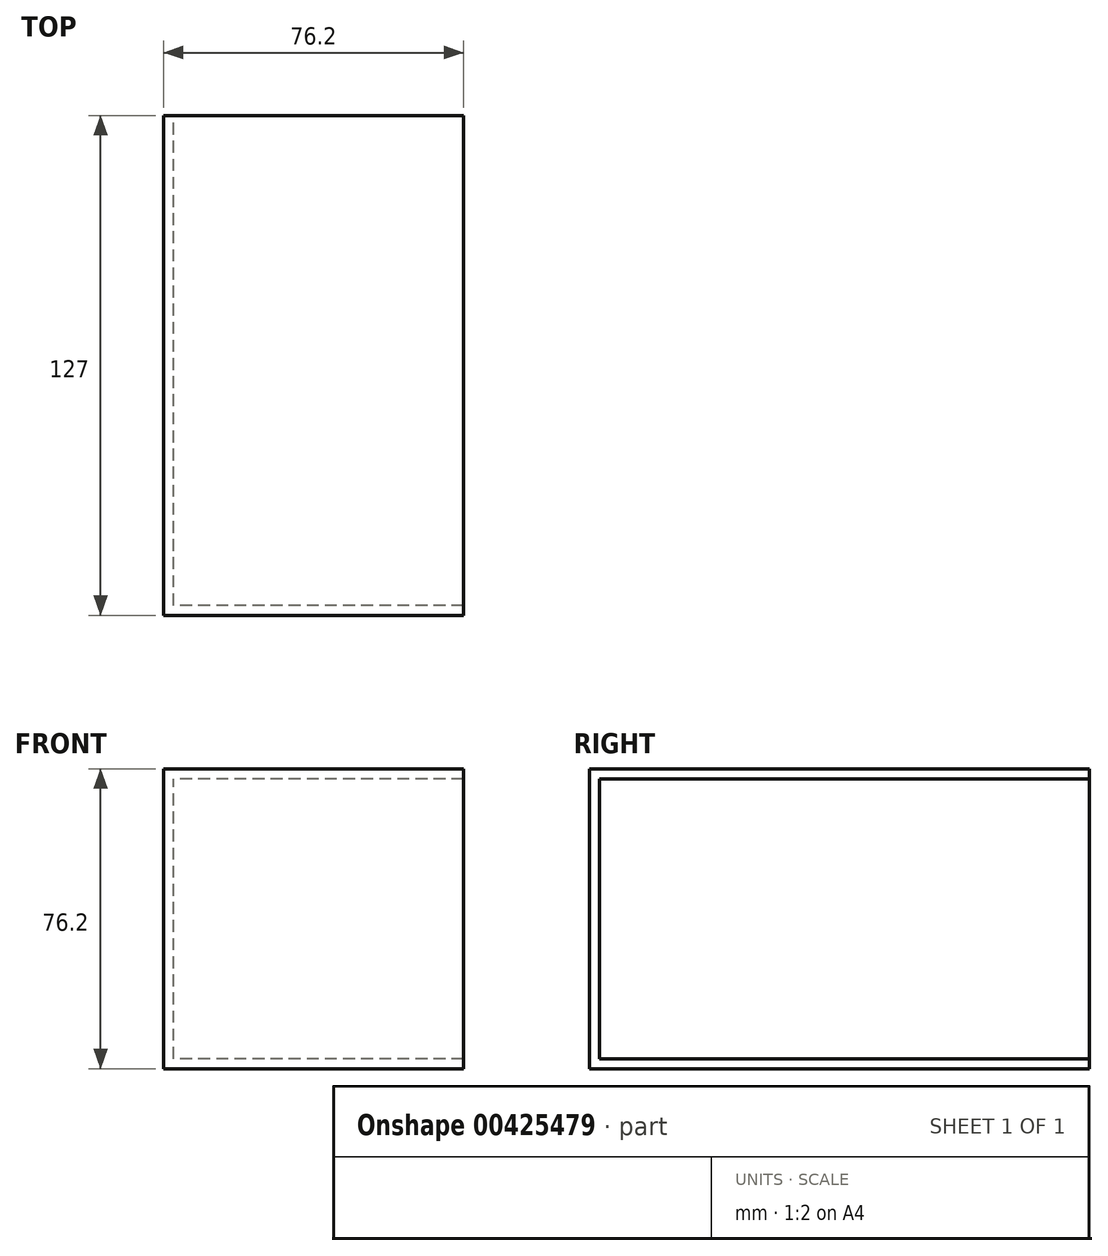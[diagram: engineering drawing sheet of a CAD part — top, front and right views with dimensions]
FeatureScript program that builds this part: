
annotation { "Feature Type Name" : "Feature", "Feature Type Description" : "" }
export const myFeature = defineFeature(function(context is Context, id is Id, definition is map)
    precondition{}
    {
        {
            var Q0;
            Q0=qCreatedBy(makeId("Front.planeOp"),FACE);
            var sketch = newSketch(context, id + "F0", { "sketchPlane" : qUnion([Q0])});
            skLineSegment(sketch, "E0.bottom", {"start": v(0, 0) * mm, "end": v(-76.2, 0) * mm});
            skLineSegment(sketch, "E0.top", {"start": v(0, 76.2) * mm, "end": v(-76.2, 76.2) * mm});
            skLineSegment(sketch, "E0.left", {"start": v(0, 0) * mm, "end": v(0, 76.2) * mm});
            skLineSegment(sketch, "E0.right", {"start": v(-76.2, 0) * mm, "end": v(-76.2, 76.2) * mm});
            skSolve(sketch);
        }
        {
            var Q0;
            Q0=makeQuery(id+"F0.imprint","IMPRINT",FACE,{"disambiguationData":[TD([[makeQuery(id+"F0.imprint","IMPRINT",EDGE,{"derivedFrom":sQuery(id+"F0.wireOp",EDGE,"E0.bottom")}),-1.0]])]});
            extrude(context, id + "F1", {"entities" : qUnion([Q0]), "depth" : 127 * mm});
        }
        {
            var Q0;
            Q0=makeQuery(id+"F1.opExtrude","CAP_FACE",FACE,{"disambiguationData":[OSD([sQuery(id+"F0.wireOp",EDGE,"E0.bottom"),sQuery(id+"F0.wireOp",EDGE,"E0.top"),sQuery(id+"F0.wireOp",EDGE,"E0.left"),sQuery(id+"F0.wireOp",EDGE,"E0.right")])],"isStart":true});
            var Q1;
            Q1=makeQuery(id+"F1.opExtrude","SWEPT_FACE",FACE,{"disambiguationData":[OSD([sQuery(id+"F0.wireOp",EDGE,"E0.left")])]});
            shell(context, id + "F2", {"entities" : qUnion([Q0, Q1]), "thickness" : 2.54 * mm});
        }
    });
